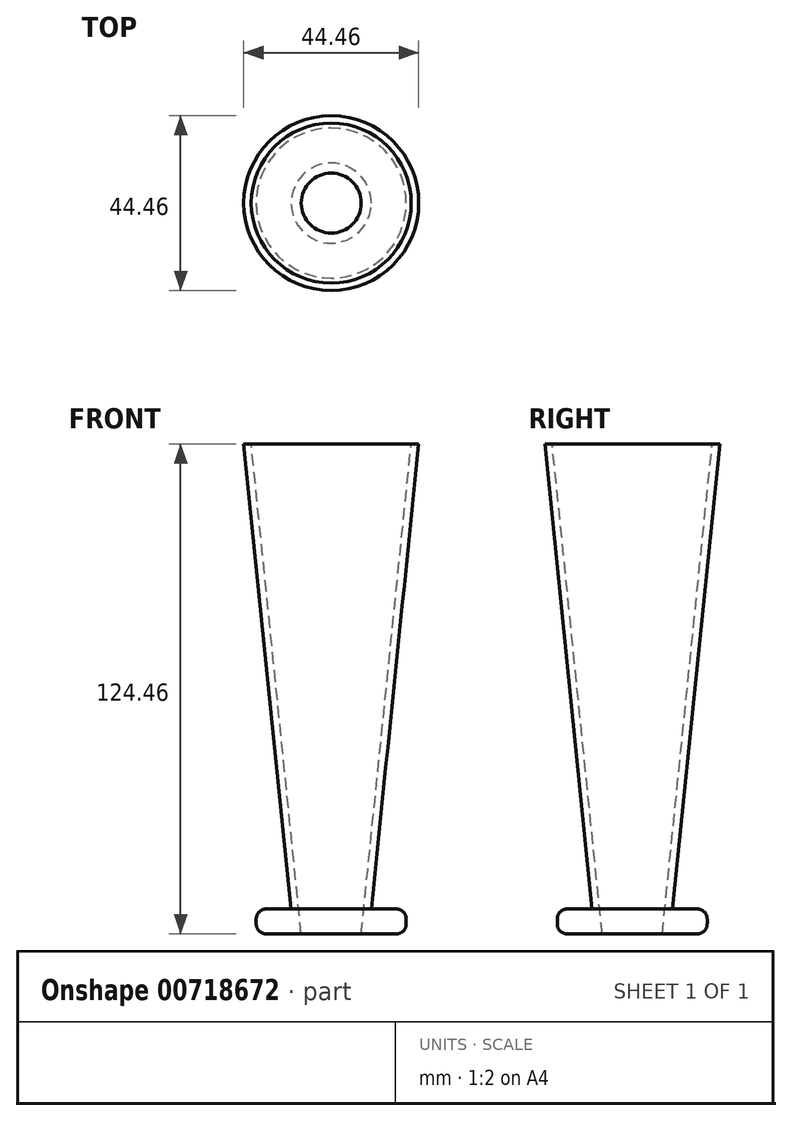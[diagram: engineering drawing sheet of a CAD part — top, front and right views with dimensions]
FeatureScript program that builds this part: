
annotation { "Feature Type Name" : "Feature", "Feature Type Description" : "" }
export const myFeature = defineFeature(function(context is Context, id is Id, definition is map)
    precondition{}
    {
        {
            var Q0;
            Q0=qCreatedBy(makeId("Top.planeOp"),FACE);
            var sketch = newSketch(context, id + "F0", { "sketchPlane" : qUnion([Q0])});
            skCircle(sketch, "E0", {"center": v(0, 0) * mm, "radius": 9.53 * mm});
            skSolve(sketch);
        }
        {
            var Q0;
            Q0=qCreatedBy(makeId("Top.planeOp"),FACE);
            cPlane(context, id + "F1", {"entities" : qUnion([Q0]), "cplaneType" : CPlaneType.OFFSET, "offset" : 124.46 * mm, "width" : 152.4 * mm, "height" : 152.4 * mm});
        }
        {
            var Q0;
            Q0=qCreatedBy(id+"F1.planeOp",FACE);
            var sketch = newSketch(context, id + "F2", { "sketchPlane" : qUnion([Q0])});
            skCircle(sketch, "E1", {"center": v(0, 0) * mm, "radius": 22.23 * mm});
            skSolve(sketch);
        }
        {
            var Q0;
            Q0=makeQuery(id+"F0.imprint","IMPRINT",FACE,{"disambiguationData":[TD([[makeQuery(id+"F0.imprint","IMPRINT",EDGE,{"derivedFrom":sQuery(id+"F0.wireOp",EDGE,"E0")}),1.0]])]});
            var Q1;
            Q1=makeQuery(id+"F2.imprint","IMPRINT",FACE,{"disambiguationData":[TD([[makeQuery(id+"F2.imprint","IMPRINT",EDGE,{"derivedFrom":sQuery(id+"F2.wireOp",EDGE,"E1")}),1.0]])]});
            loft(context, id + "F3", {"sheetProfilesArray" : [{ "sheetProfileEntities" : qUnion([Q0]) }, { "sheetProfileEntities" : qUnion([Q1]) }]});
        }
        {
            var Q0;
            Q0=makeQuery(id+"F3.opLoft","CAP_FACE",FACE,{"disambiguationData":[OSD([makeQuery(id+"F2.imprint","IMPRINT",FACE,{"disambiguationData":[TD([[makeQuery(id+"F2.imprint","IMPRINT",EDGE,{"derivedFrom":sQuery(id+"F2.wireOp",EDGE,"E1")}),1.0]])]})])],"isStart":true});
            var sketch = newSketch(context, id + "F4", { "sketchPlane" : qUnion([Q0])});
            skCircle(sketch, "E2", {"center": v(0, 0) * mm, "radius": 20.32 * mm});
            skSolve(sketch);
        }
        {
            var Q0;
            Q0=makeQuery(id+"F3.opLoft","CAP_FACE",FACE,{"disambiguationData":[OSD([makeQuery(id+"F0.imprint","IMPRINT",FACE,{"disambiguationData":[TD([[makeQuery(id+"F0.imprint","IMPRINT",EDGE,{"derivedFrom":sQuery(id+"F0.wireOp",EDGE,"E0")}),1.0]])]})])],"isStart":true});
            var sketch = newSketch(context, id + "F5", { "sketchPlane" : qUnion([Q0])});
            skCircle(sketch, "E3", {"center": v(0, 0) * mm, "radius": 7.62 * mm});
            skSolve(sketch);
        }
        {
            var Q0;
            Q0=qCreatedBy(makeId("Top.planeOp"),FACE);
            var sketch = newSketch(context, id + "F6", { "sketchPlane" : qUnion([Q0])});
            skCircle(sketch, "E4", {"center": v(0, 0) * mm, "radius": 19.05 * mm});
            skSolve(sketch);
        }
        {
            var Q0;
            Q0=makeQuery(id+"F6.imprint","IMPRINT",FACE,{"disambiguationData":[TD([[makeQuery(id+"F6.imprint","IMPRINT",EDGE,{"derivedFrom":sQuery(id+"F6.wireOp",EDGE,"E4")}),1.0]])]});
            extrude(context, id + "F7", {"entities" : qUnion([Q0]), "operationType" : NewBodyOperationType.ADD, "depth" : 6.35 * mm, "offsetDistance" : 25.4 * mm});
        }
        {
            var Q1;
            Q1=makeQuery(id+"F5.imprint","IMPRINT",FACE,{"disambiguationData":[TD([[makeQuery(id+"F5.imprint","IMPRINT",EDGE,{"derivedFrom":sQuery(id+"F5.wireOp",EDGE,"E3")}),1.0]])]});
            var Q2;
            Q2=makeQuery(id+"F4.imprint","IMPRINT",FACE,{"disambiguationData":[TD([[makeQuery(id+"F4.imprint","IMPRINT",EDGE,{"derivedFrom":sQuery(id+"F4.wireOp",EDGE,"E2")}),1.0]])]});
            loft(context, id + "F8", {"operationType" : NewBodyOperationType.REMOVE, "sheetProfilesArray" : [{ "sheetProfileEntities" : qUnion([Q1]) }, { "sheetProfileEntities" : qUnion([Q2]) }]});
        }
        {
            var Q0;
            Q0=makeQuery(id+"F7.opExtrude","CAP_EDGE",EDGE,{"disambiguationData":[OSD([sQuery(id+"F6.wireOp",EDGE,"E4")])],"isStart":false});
            var Q1;
            Q1=makeQuery(id+"F7.opExtrude","CAP_EDGE",EDGE,{"disambiguationData":[OSD([sQuery(id+"F6.wireOp",EDGE,"E4")])],"isStart":true});
            fillet(context, id + "F9", {"entities" : qUnion([Q0, Q1]), "radius" : 2.54 * mm, "tangentPropagation" : true, "allowEdgeOverflow" : false});
        }
    });
